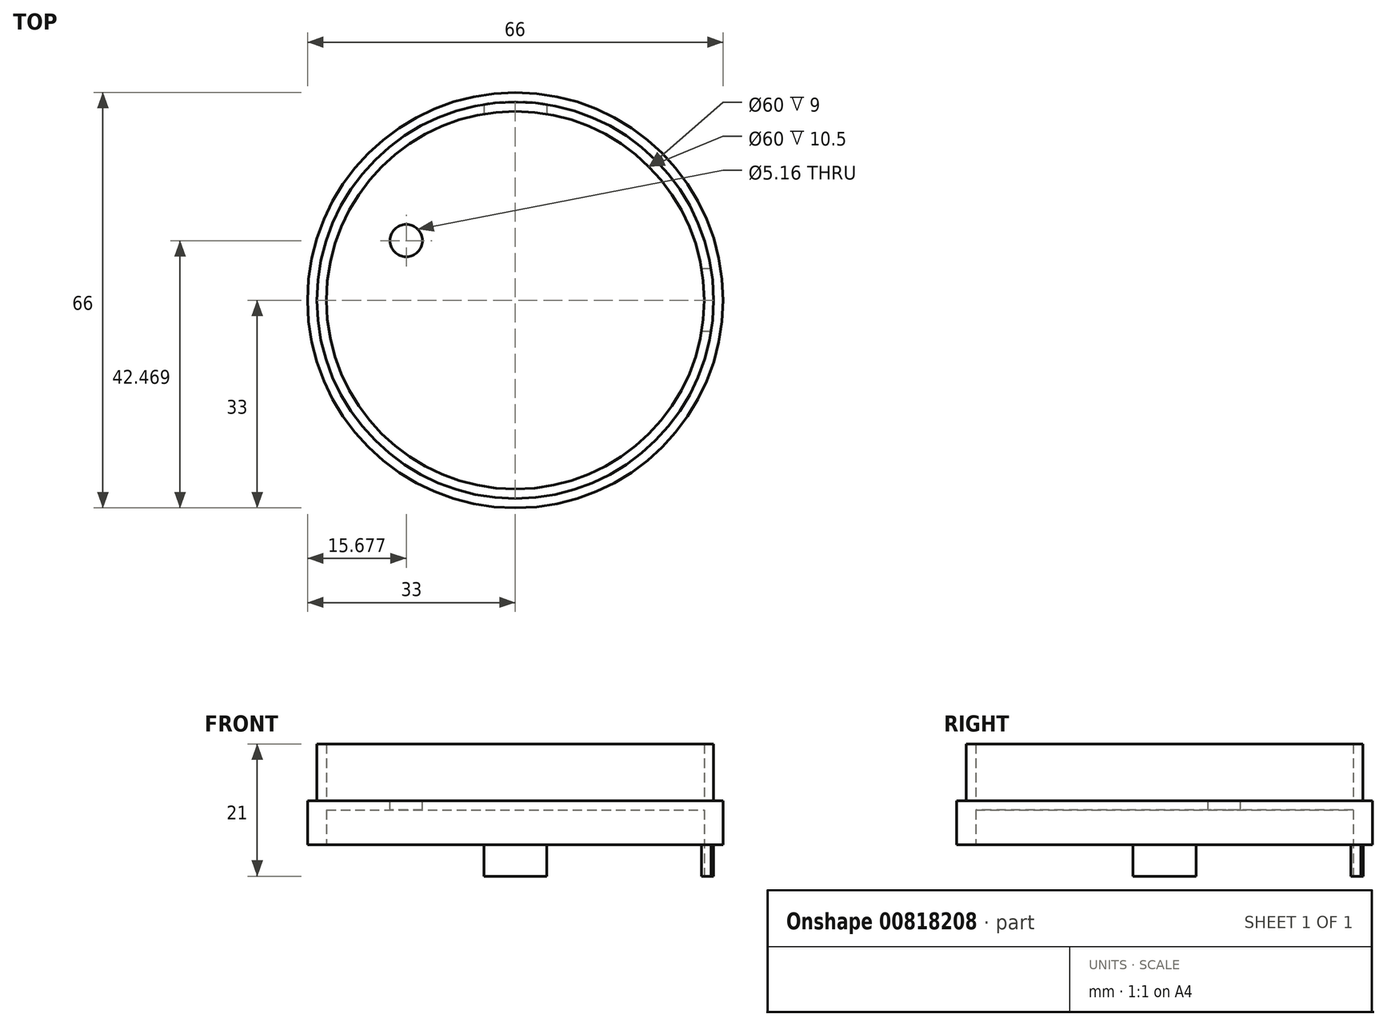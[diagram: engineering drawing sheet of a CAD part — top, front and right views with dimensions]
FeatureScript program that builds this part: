
annotation { "Feature Type Name" : "Feature", "Feature Type Description" : "" }
export const myFeature = defineFeature(function(context is Context, id is Id, definition is map)
    precondition{}
    {
        {
            var Q0;
            Q0=qCreatedBy(makeId("Front.planeOp"),FACE);
            var sketch = newSketch(context, id + "F0", { "sketchPlane" : qUnion([Q0])});
            skLineSegment(sketch, "E0", {"start": v(0, 0) * mm, "end": v(30, 0) * mm});
            skLineSegment(sketch, "E1", {"start": v(30, 0) * mm, "end": v(30, 9) * mm});
            skLineSegment(sketch, "E2", {"start": v(30, 9) * mm, "end": v(31.5, 9) * mm});
            skLineSegment(sketch, "E3", {"start": v(31.5, 9) * mm, "end": v(31.5, 0) * mm});
            skLineSegment(sketch, "E4", {"start": v(31.5, 0) * mm, "end": v(33, 0) * mm});
            skLineSegment(sketch, "E5", {"start": v(33, 0) * mm, "end": v(33, -12) * mm});
            skLineSegment(sketch, "E6", {"start": v(33, -12) * mm, "end": v(30, -12) * mm});
            skLineSegment(sketch, "E7", {"start": v(30, -12) * mm, "end": v(30, -1.5) * mm});
            skLineSegment(sketch, "E8", {"start": v(30, -1.5) * mm, "end": v(0, -1.5) * mm});
            skLineSegment(sketch, "E9", {"start": v(0, -1.5) * mm, "end": v(0, 0) * mm});
            skSolve(sketch);
        }
        {
            var Q0;
            Q0 = qSketchRegion(id + "F0", true);
            var Q1;
            Q1=sQuery(id+"F0.wireOp",EDGE,"E9");
            revolve(context, id + "F1", {"surfaceOperationType" : NewSurfaceOperationType.NEW, "entities" : qUnion([Q0]), "axis" : qUnion([Q1]), "revolveType" : RevolveType.FULL});
        }
        {
            var Q0;
            Q0=makeQuery(id+"F1.opRevolve","SWEPT_FACE",FACE,{"disambiguationData":[OSD([sQuery(id+"F0.wireOp",EDGE,"E6")])]});
            var sketch = newSketch(context, id + "F2", { "sketchPlane" : qUnion([Q0])});
            skLineSegment(sketch, "E10.left", {"start": v(-35, 5.01) * mm, "end": v(-35, -4.99) * mm, "construction": true});
            skLineSegment(sketch, "E10.right", {"start": v(35, 5.01) * mm, "end": v(35, -4.99) * mm, "construction": true});
            skArc(sketch, "E11", {"start": v(-31.1, 4.99) * mm, "mid": v(-31.5, 0) * mm, "end": v(-31.1, -4.99) * mm});
            skLineSegment(sketch, "E12", {"start": v(-31.1, 4.99) * mm, "end": v(0, 4.99) * mm});
            skLineSegment(sketch, "E13", {"start": v(-31.1, -4.99) * mm, "end": v(0, -4.99) * mm});
            skArc(sketch, "E14.MirrorCS", {"start": v(31.1, 4.99) * mm, "mid": v(31.5, 0) * mm, "end": v(31.1, -4.99) * mm});
            skLineSegment(sketch, "E15.MirrorCS", {"start": v(31.1, 4.99) * mm, "end": v(0, 4.99) * mm});
            skLineSegment(sketch, "E16.MirrorCS", {"start": v(31.1, -4.99) * mm, "end": v(0, -4.99) * mm});
            skArc(sketch, "E17", {"start": v(5, 31.03) * mm, "mid": v(0, 31.43) * mm, "end": v(-5, 31.03) * mm});
            skLineSegment(sketch, "E18", {"start": v(5, 31.03) * mm, "end": v(5, -0.07) * mm});
            skLineSegment(sketch, "E19", {"start": v(-5, 31.03) * mm, "end": v(-5, -0.07) * mm});
            skArc(sketch, "E20.MirrorCS", {"start": v(5, -31.17) * mm, "mid": v(0, -31.57) * mm, "end": v(-5, -31.17) * mm});
            skLineSegment(sketch, "E21.MirrorCS", {"start": v(5, -31.17) * mm, "end": v(5, -0.07) * mm});
            skLineSegment(sketch, "E22.MirrorCS", {"start": v(-5, -31.17) * mm, "end": v(-5, -0.07) * mm});
            skSolve(sketch);
        }
        {
            var Q0;
            {var subQ0=sQuery(id+"F2.wireOp",EDGE,"E17");Q0=makeQuery(id+"F2.imprint","IMPRINT",FACE,{"disambiguationData":[TD([[makeQuery(id+"F2.imprint","IMPRINT",EDGE,{"derivedFrom":subQ0}),1.0]])]});}
            var Q1;
            {var subQ0=sQuery(id+"F2.wireOp",EDGE,"E11");Q1=makeQuery(id+"F2.imprint","IMPRINT",FACE,{"disambiguationData":[TD([[makeQuery(id+"F2.imprint","IMPRINT",EDGE,{"derivedFrom":subQ0}),1.0]])]});}
            var Q2;
            {var subQ0=sQuery(id+"F2.wireOp",EDGE,"E20.MirrorCS");Q2=makeQuery(id+"F2.imprint","IMPRINT",FACE,{"disambiguationData":[TD([[makeQuery(id+"F2.imprint","IMPRINT",EDGE,{"derivedFrom":subQ0}),-1.0]])]});}
            var Q3;
            {var subQ0=sQuery(id+"F2.wireOp",EDGE,"E14.MirrorCS");Q3=makeQuery(id+"F2.imprint","IMPRINT",FACE,{"disambiguationData":[TD([[makeQuery(id+"F2.imprint","IMPRINT",EDGE,{"derivedFrom":subQ0}),-1.0]])]});}
            extrude(context, id + "F3", {"entities" : qUnion([Q0, Q1, Q2, Q3]), "operationType" : NewBodyOperationType.REMOVE, "oppositeDirection" : true, "depth" : 5 * mm, "offsetDistance" : 25 * mm});
        }
        {
            var Q0;
            Q0=makeQuery(id+"F1.opRevolve","SWEPT_FACE",FACE,{"disambiguationData":[OSD([sQuery(id+"F0.wireOp",EDGE,"E2")])]});
            var sketch = newSketch(context, id + "F4", { "sketchPlane" : qUnion([Q0])});
            skCircle(sketch, "E23", {"center": v(-17.32, 9.47) * mm, "radius": 2.58 * mm});
            skSolve(sketch);
        }
        {
            var Q0;
            Q0 = qSketchRegion(id + "F4", true);
            extrude(context, id + "F5", {"entities" : qUnion([Q0]), "operationType" : NewBodyOperationType.REMOVE, "oppositeDirection" : true, "depth" : 25 * mm, "offsetDistance" : 25 * mm});
        }
    });
